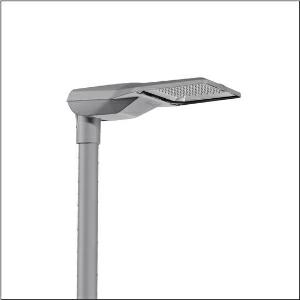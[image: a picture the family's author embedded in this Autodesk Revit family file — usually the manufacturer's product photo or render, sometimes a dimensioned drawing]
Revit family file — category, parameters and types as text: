
# Revit family: streetlight_sl_21_iq_midi___pc-l_5xe3f41g08mb_febf
name_source: partatom
category: Lighting Fixtures
units: mm (PartAtom-declared; Revit-internal decimal feet)

## family parameters
Cut with Voids When Loaded = No
Host = Face
Light Source = No
Part Type = Normal
Room Calculation Point = No
Round Connector Dimension = Use Diameter
Shared = No

## types (1)
- --- (1 x LED, 19370 lm, 146.7 W, 4000K)
    Apparent Load = 147 VA
    CIE Flux Codes = 38 78 98 100 100
    Color Rendering = 70
    Color Temperature = 4000K
    Default Elevation = 1800 mm
    Description = Streetlight SL 21 iQ midi, mast luminaire, primary light control with lens, of PMMA, primary optical cover: cover, of toughened safety glass, transparent, light distribution: PC-L, light emission: direct distribution, primary light characteristic: asymmetric, left, installation type: post-top, side-entry, LED, High Power LED, rated luminous flux: 19.370lm, luminous efficacy: 132lm/W, light colour: 740, colour temperature: 4000K, control: Street-Remote, Auto-Match, Temp-Guard, Lumen-Switch, Night-Set, Smart-Wire, Light-Fading, Desk-Remote (wireless, voltage-free reading and setting of iQ features in the workshop via application-optimized NFC function/RFID function), optimised constant luminous flux control (CLO 2.0), pre-setting: linear dimming characteristic, mains connection: 230..240V, AC, 50/60Hz, start of lifetime: 147W, end of service life: 161W, reduction: 62W, luminaire housing, of diecast aluminium, powder-coated, Siteco® metallic grey (DB 702S), corrosivity category C5 mid according to DIN EN ISO 12944, please order mast flange separately, inclination adjustable: 0°, 5°, 10°, 15°, sealing non-destructively replaceable, multi-level sealing system, length: 644mm, width: 335mm, height: 110mm, mast flange for spigot size: 42mm (side-entry): 5XC10008XM4, 60/48mm (side-entry/post-top): 5XC10108XM2, 76/60mm (side-entry/post-top): 5XC10108XM1, protection rating (complete): IP66, insulation class (complete): insulation class II (safety insulation), certification: CE, ENEC, ENEC+, VDE, impact resistance: IK09, permissible operating ambient temperature for outdoor applications: -40..+50°C, standard-compliant lighting for roads and squares, packaging unit: 1 piece

Light Distribution: PC-L
    Height = 111 mm
    Lamp = 1 x LED
    Lamp Light Flux = 19370 lm
    Lamp Power = 146.7 W
    Lamp count = 1
    Length = 644 mm
    Luminous efficacy = 132 lm/W
    Manufacturer = Siteco
    ModVariant = No
    Model = 5XE3F41G08MB
    Number of Poles = 1
    OnlyDefault = Yes
    Power Factor = 1
    Product Name = Streetlight SL 21 iQ midi | PC-L
    Product group = mast luminaire | pylon top
    ProductGroupID = 6100
    Protection Class = Protection class II
    Protection Degree = IP 66
    RLX_Detail_Level = 1
    RLX_Emergency_Light_Flux = 0 lm
    RLX_Emergency_Type = 0
    RLX_Emergency_Type_DB = No
    RlxData = <blob elided: 93069 chars, md5=65bdb126>
    Socket = socket
    Standby Power = 0 W
    System Light Flux = 19370 lm
    System Power = 147 W
    Type Comments = factory setting: luminous flux: 100 % | dim-lin: 254 | 753 mA
    Type Image = l_1004298.jpg
    URL = http://relux.com
    VarID = @adj_032535
    Voltage = 0 V
    Weight = 0.00 kg
    Width = 336 mm

## geometry (parser evidence)
native form markers: Blend x4, Sweep x11
no freeform markers — native parametric forms only
